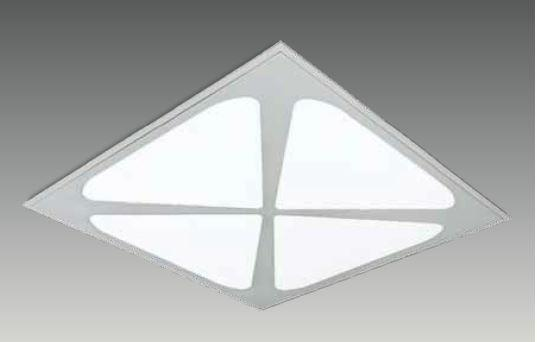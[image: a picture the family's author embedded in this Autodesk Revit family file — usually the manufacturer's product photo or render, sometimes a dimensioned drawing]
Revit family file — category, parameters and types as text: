
# Revit family: G 6060 CLO
name_source: partatom
category: Lighting Fixtures
revit_build: Autodesk Revit 2017 (Build: 20160225_1515(x64)
units: mm (PartAtom-declared; Revit-internal decimal feet)

## family parameters
Always vertical = Yes
Cut with Voids When Loaded = No
Host = Ceiling
Light Source = Yes
OmniClass Number = 23.80.70.11
OmniClass Title = Luminaries for Internal Lighting
Part Type = Normal
Room Calculation Point = No
Round Connector Dimension = Use Diameter
Shared = No

## types (4) — shared parameters
Color Filter = 16777215
Dimming Lamp Color Temperature Shift = <None>
Emit Shape Visible in Rendering = Yes
Emit from Rectangle Length = 570 mm  [stored 1.87008 ft]
Emit from Rectangle Width = 570 mm  [stored 1.87008 ft]
Light Source Symbol Size = 610 mm
Manufacturer = ARLIGHT
Type Image = G 6060 CLO.JPG

## per-type parameters (varying)
| type | Wattage Comments |
| GCLO.6060.36.30 | 36 |
| GCLO.6060.36.40 | 36 |
| GCLO.6060.28.30 | 28 |
| GCLO.6060.28.40 | 28 |

note: [stored X ft] marks values corroborated as IEEE doubles in the binary element streams (Revit-internal decimal feet)

## geometry (parser evidence)
native form markers: Sweep x2
no freeform markers — native parametric forms only
